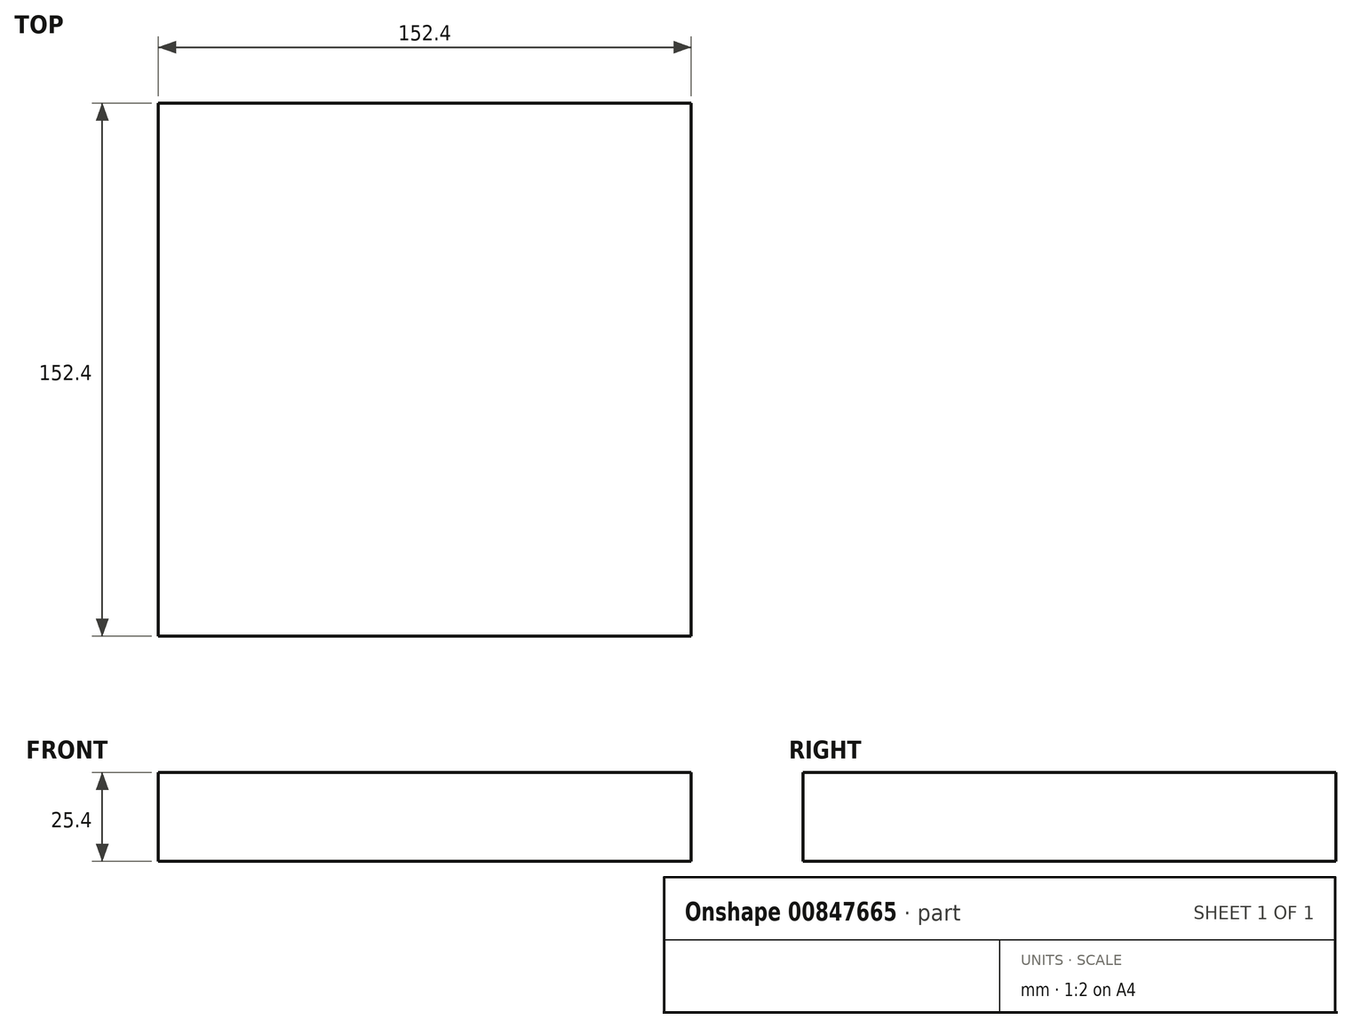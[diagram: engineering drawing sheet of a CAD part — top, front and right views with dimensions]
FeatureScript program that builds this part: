
annotation { "Feature Type Name" : "Feature", "Feature Type Description" : "" }
export const myFeature = defineFeature(function(context is Context, id is Id, definition is map)
    precondition{}
    {
        {
            var Q0;
            Q0=qCreatedBy(makeId("Top.planeOp"),FACE);
            var sketch = newSketch(context, id + "F0", { "sketchPlane" : qUnion([Q0])});
            skLineSegment(sketch, "E0.bottom", {"start": v(76.2, -74.12) * mm, "end": v(-76.2, -74.12) * mm});
            skLineSegment(sketch, "E0.top", {"start": v(76.2, 78.28) * mm, "end": v(-76.2, 78.28) * mm});
            skLineSegment(sketch, "E0.left", {"start": v(76.2, -74.12) * mm, "end": v(76.2, 78.28) * mm});
            skLineSegment(sketch, "E0.right", {"start": v(-76.2, -74.12) * mm, "end": v(-76.2, 78.28) * mm});
            skPoint(sketch, "E0.middle", {"position": v(0, 2.08) * mm});
            skSolve(sketch);
        }
        {
            var Q0;
            Q0=makeQuery(id+"F0.imprint","IMPRINT",FACE,{"disambiguationData":[TD([[makeQuery(id+"F0.imprint","IMPRINT",EDGE,{"derivedFrom":sQuery(id+"F0.wireOp",EDGE,"E0.bottom")}),-1.0]])]});
            extrude(context, id + "F1", {"entities" : qUnion([Q0]), "depth" : 25.4 * mm, "offsetDistance" : 25.4 * mm});
        }
    });
